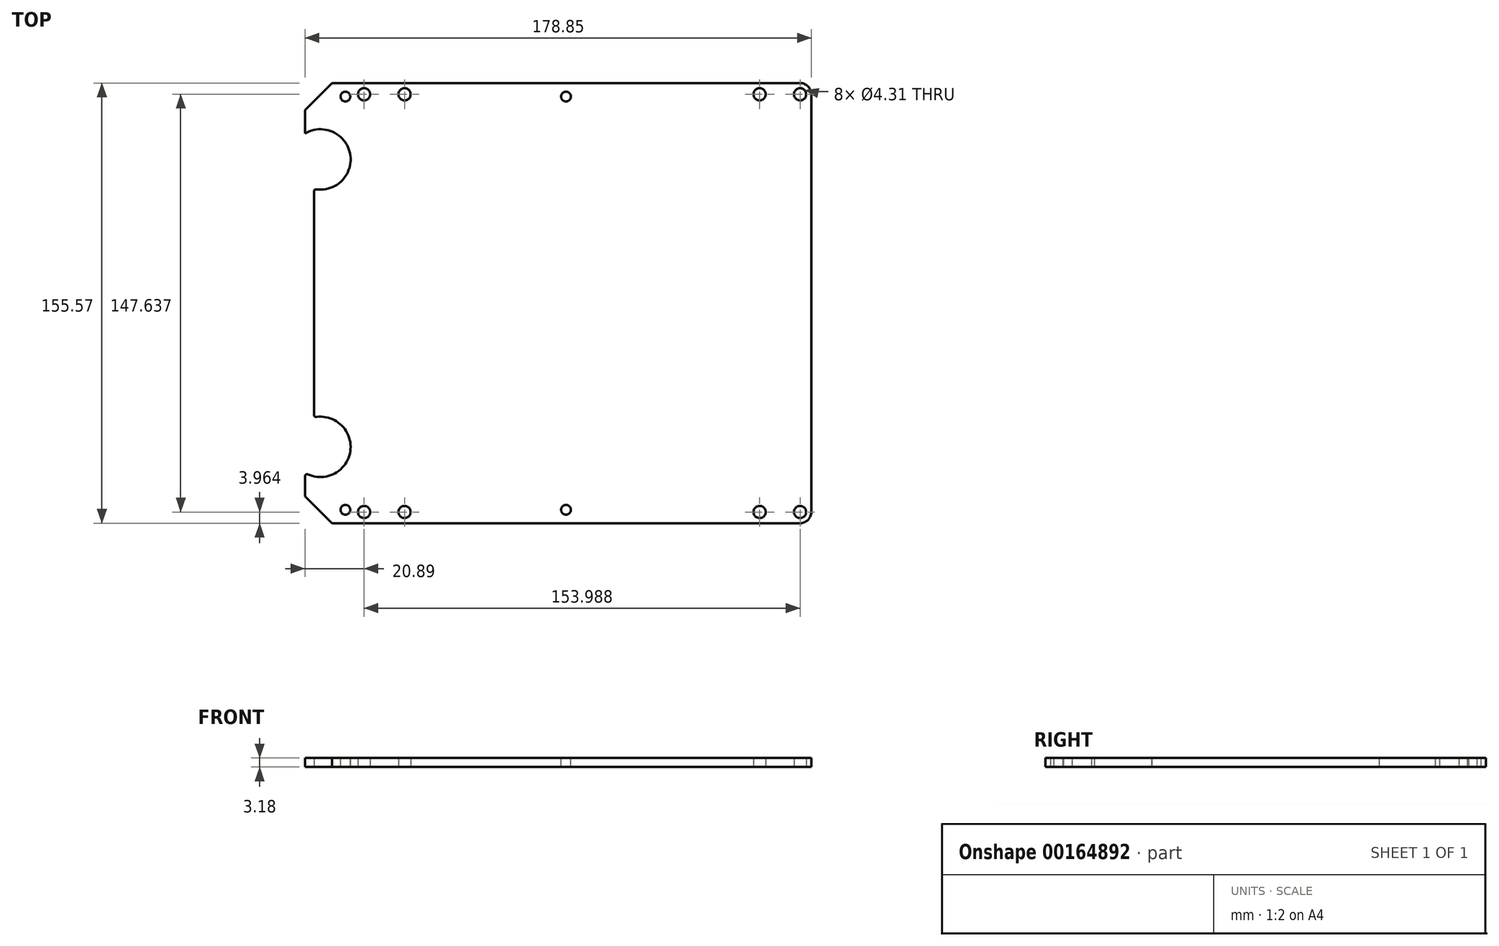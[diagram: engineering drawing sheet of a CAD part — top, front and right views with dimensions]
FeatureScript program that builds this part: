
annotation { "Feature Type Name" : "Feature", "Feature Type Description" : "" }
export const myFeature = defineFeature(function(context is Context, id is Id, definition is map)
    precondition{}
    {
        {
            var Q0;
            Q0=qCreatedBy(makeId("Top.planeOp"),FACE);
            var sketch = newSketch(context, id + "F0", { "sketchPlane" : qUnion([Q0])});
            skLineSegment(sketch, "E0.bottom", {"start": v(0, 0) * mm, "end": v(178.85, 0) * mm});
            skLineSegment(sketch, "E0.top", {"start": v(0, -155.58) * mm, "end": v(178.85, -155.58) * mm});
            skLineSegment(sketch, "E0.left", {"start": v(0, 0) * mm, "end": v(0, -155.57) * mm});
            skLineSegment(sketch, "E0.right", {"start": v(178.85, 0) * mm, "end": v(178.85, -155.58) * mm});
            skLineSegment(sketch, "E1.bottom", {"start": v(160.6, -151.6) * mm, "end": v(174.88, -151.6) * mm, "construction": true});
            skLineSegment(sketch, "E1.top", {"start": v(160.6, -3.97) * mm, "end": v(174.88, -3.97) * mm, "construction": true});
            skLineSegment(sketch, "E1.left", {"start": v(160.6, -151.6) * mm, "end": v(160.6, -3.97) * mm, "construction": true});
            skLineSegment(sketch, "E1.right", {"start": v(174.88, -151.6) * mm, "end": v(174.88, -3.97) * mm, "construction": true});
            skPoint(sketch, "E1.middle", {"position": v(167.73, -77.79) * mm});
            skLineSegment(sketch, "E2.bottom", {"start": v(20.9, -3.97) * mm, "end": v(35.18, -3.97) * mm, "construction": true});
            skLineSegment(sketch, "E2.top", {"start": v(20.9, -151.6) * mm, "end": v(35.18, -151.6) * mm, "construction": true});
            skLineSegment(sketch, "E2.left", {"start": v(20.9, -3.97) * mm, "end": v(20.9, -151.6) * mm, "construction": true});
            skLineSegment(sketch, "E2.right", {"start": v(35.18, -3.97) * mm, "end": v(35.18, -151.6) * mm, "construction": true});
            skPoint(sketch, "E2.middle", {"position": v(28.03, -77.79) * mm});
            skLineSegment(sketch, "E3", {"start": v(28.03, -77.79) * mm, "end": v(97.88, -77.79) * mm, "construction": true});
            skLineSegment(sketch, "E4", {"start": v(97.88, -77.79) * mm, "end": v(97.88, -155.58) * mm, "construction": true});
            skLineSegment(sketch, "E5", {"start": v(97.88, -77.79) * mm, "end": v(97.88, 0) * mm, "construction": true});
            skLineSegment(sketch, "E6", {"start": v(97.88, -77.79) * mm, "end": v(167.73, -77.79) * mm, "construction": true});
            skLineSegment(sketch, "E7", {"start": v(174.88, -3.97) * mm, "end": v(174.88, 0) * mm, "construction": true});
            skLineSegment(sketch, "E8", {"start": v(174.88, -3.97) * mm, "end": v(178.85, -3.97) * mm, "construction": true});
            skCircle(sketch, "E9", {"center": v(20.9, -3.97) * mm, "radius": 2.15 * mm});
            skCircle(sketch, "E10", {"center": v(35.18, -3.97) * mm, "radius": 2.15 * mm});
            skCircle(sketch, "E11", {"center": v(174.88, -3.97) * mm, "radius": 2.15 * mm});
            skCircle(sketch, "E12", {"center": v(160.6, -3.97) * mm, "radius": 2.15 * mm});
            skCircle(sketch, "E13", {"center": v(160.6, -151.6) * mm, "radius": 2.15 * mm});
            skCircle(sketch, "E14", {"center": v(174.88, -151.6) * mm, "radius": 2.15 * mm});
            skCircle(sketch, "E15", {"center": v(20.9, -151.6) * mm, "radius": 2.15 * mm});
            skCircle(sketch, "E16", {"center": v(35.18, -151.6) * mm, "radius": 2.15 * mm});
            skSolve(sketch);
        }
        {
            var Q0;
            Q0 = qSketchRegion(id + "F0", true);
            extrude(context, id + "F1", {"entities" : qUnion([Q0]), "depth" : 3.17 * mm});
        }
        {
            var Q0;
            Q0=makeQuery(id+"F1.opExtrude","SWEPT_EDGE",EDGE,{"disambiguationData":[OSD([sQuery(id+"F0.wireOp",EDGE,"E0.bottom"),sQuery(id+"F0.wireOp",EDGE,"E0.right")])]});
            var Q1;
            Q1=makeQuery(id+"F1.opExtrude","SWEPT_EDGE",EDGE,{"disambiguationData":[OSD([sQuery(id+"F0.wireOp",EDGE,"E0.top"),sQuery(id+"F0.wireOp",EDGE,"E0.right")])]});
            fillet(context, id + "F2", {"entities" : qUnion([Q0, Q1]), "radius" : 3.97 * mm, "tangentPropagation" : true, "allowEdgeOverflow" : false});
        }
        {
            var Q0;
            Q0=makeQuery(id+"F1.opExtrude","CAP_FACE",FACE,{"disambiguationData":[OSD([sQuery(id+"F0.wireOp",EDGE,"E0.bottom"),sQuery(id+"F0.wireOp",EDGE,"E0.top"),sQuery(id+"F0.wireOp",EDGE,"E0.left"),sQuery(id+"F0.wireOp",EDGE,"E0.right"),sQuery(id+"F0.wireOp",EDGE,"E9"),sQuery(id+"F0.wireOp",EDGE,"E10"),sQuery(id+"F0.wireOp",EDGE,"E11"),sQuery(id+"F0.wireOp",EDGE,"E12"),sQuery(id+"F0.wireOp",EDGE,"E13"),sQuery(id+"F0.wireOp",EDGE,"E14"),sQuery(id+"F0.wireOp",EDGE,"E15"),sQuery(id+"F0.wireOp",EDGE,"E16")])],"isStart":false});
            var sketch = newSketch(context, id + "F3", { "sketchPlane" : qUnion([Q0])});
            skLineSegment(sketch, "E17", {"start": v(5.45, -77.79) * mm, "end": v(0, -77.79) * mm, "construction": true});
            skLineSegment(sketch, "E18", {"start": v(5.45, -26.99) * mm, "end": v(5.45, -128.59) * mm, "construction": true});
            skArc(sketch, "E19", {"start": v(0, -137.76) * mm, "mid": v(16, -130.3) * mm, "end": v(3.18, -118.16) * mm});
            skLineSegment(sketch, "E20", {"start": v(0, -17.81) * mm, "end": v(0, -137.76) * mm});
            skArc(sketch, "E21", {"start": v(3.17, -37.42) * mm, "mid": v(16, -25.28) * mm, "end": v(0, -17.81) * mm});
            skLineSegment(sketch, "E22", {"start": v(5.45, -128.59) * mm, "end": v(0, -128.59) * mm, "construction": true});
            skLineSegment(sketch, "E23", {"start": v(3.17, -37.42) * mm, "end": v(3.18, -118.16) * mm});
            skSolve(sketch);
        }
        {
            var Q0;
            Q0 = qSketchRegion(id + "F3", true);
            var Q1;
            Q1=makeQuery(id+"F1.opExtrude","CAP_FACE",FACE,{"disambiguationData":[OSD([sQuery(id+"F0.wireOp",EDGE,"E0.bottom"),sQuery(id+"F0.wireOp",EDGE,"E0.top"),sQuery(id+"F0.wireOp",EDGE,"E0.left"),sQuery(id+"F0.wireOp",EDGE,"E0.right"),sQuery(id+"F0.wireOp",EDGE,"E9"),sQuery(id+"F0.wireOp",EDGE,"E10"),sQuery(id+"F0.wireOp",EDGE,"E11"),sQuery(id+"F0.wireOp",EDGE,"E12"),sQuery(id+"F0.wireOp",EDGE,"E13"),sQuery(id+"F0.wireOp",EDGE,"E14"),sQuery(id+"F0.wireOp",EDGE,"E15"),sQuery(id+"F0.wireOp",EDGE,"E16")])],"isStart":true});
            extrude(context, id + "F4", {"entities" : qUnion([Q0]), "operationType" : NewBodyOperationType.REMOVE, "endBound" : BoundingType.UP_TO_SURFACE, "oppositeDirection" : true, "endBoundEntityFace" : qUnion([Q1]), "depth" : 25.4 * mm});
        }
        {
            var Q0;
            {var subQ0=sQuery(id+"F3.wireOp",EDGE,"wcZEUR4v-bPc0-u3v2-X1AI-emrUXp2CaUBA");var subQ1=sQuery(id+"F3.wireOp",EDGE,"E21");var subQ2=sQuery(id+"F0.wireOp",EDGE,"E0.left");Q0=makeQuery(id+"F4.boolean.opBoolean","COPY",EDGE,{"derivedFrom":makeQuery(id+"F4.opExtrude","SWEPT_EDGE",EDGE,{"disambiguationData":[OSD([subQ2,subQ1,subQ0]),TDD([makeQuery(id+"F3.imprint","INTERSECT",VERTEX,{"disambiguationData":[OD(1.0)],"derivedFrom":[makeQuery(id+"F1.opExtrude","CAP_EDGE",EDGE,{"disambiguationData":[OSD([subQ2])],"isStart":false}),subQ1,subQ0]})])]})});}
            var Q1;
            {var subQ0=sQuery(id+"F3.wireOp",EDGE,"wcZEUR4v-bPc0-u3v2-X1AI-emrUXp2CaUBA");var subQ1=sQuery(id+"F3.wireOp",EDGE,"E21");var subQ2=sQuery(id+"F0.wireOp",EDGE,"E0.left");Q1=makeQuery(id+"F4.boolean.opBoolean","COPY",EDGE,{"derivedFrom":makeQuery(id+"F4.opExtrude","SWEPT_EDGE",EDGE,{"disambiguationData":[OSD([subQ2,subQ1,subQ0]),TDD([makeQuery(id+"F3.imprint","INTERSECT",VERTEX,{"disambiguationData":[OD(0.0)],"derivedFrom":[makeQuery(id+"F1.opExtrude","CAP_EDGE",EDGE,{"disambiguationData":[OSD([subQ2])],"isStart":false}),subQ1,subQ0]})])]})});}
            var Q2;
            {var subQ0=sQuery(id+"F3.wireOp",EDGE,"E20");var subQ1=sQuery(id+"F3.wireOp",EDGE,"E19");var subQ2=sQuery(id+"F0.wireOp",EDGE,"E0.left");Q2=makeQuery(id+"F4.boolean.opBoolean","COPY",EDGE,{"derivedFrom":makeQuery(id+"F4.opExtrude","SWEPT_EDGE",EDGE,{"disambiguationData":[OSD([subQ2,subQ1,subQ0]),TDD([makeQuery(id+"F3.imprint","INTERSECT",VERTEX,{"disambiguationData":[OD(1.0)],"derivedFrom":[makeQuery(id+"F1.opExtrude","CAP_EDGE",EDGE,{"disambiguationData":[OSD([subQ2])],"isStart":false}),subQ1,subQ0]})])]})});}
            var Q3;
            {var subQ0=sQuery(id+"F3.wireOp",EDGE,"E20");var subQ1=sQuery(id+"F3.wireOp",EDGE,"E19");var subQ2=sQuery(id+"F0.wireOp",EDGE,"E0.left");Q3=makeQuery(id+"F4.boolean.opBoolean","COPY",EDGE,{"derivedFrom":makeQuery(id+"F4.opExtrude","SWEPT_EDGE",EDGE,{"disambiguationData":[OSD([subQ2,subQ1,subQ0]),TDD([makeQuery(id+"F3.imprint","INTERSECT",VERTEX,{"disambiguationData":[OD(0.0)],"derivedFrom":[makeQuery(id+"F1.opExtrude","CAP_EDGE",EDGE,{"disambiguationData":[OSD([subQ2])],"isStart":false}),subQ1,subQ0]})])]})});}
            var Q4;
            Q4=makeQuery(id+"F4.boolean.opBoolean","COPY",EDGE,{"derivedFrom":makeQuery(id+"F4.opExtrude","SWEPT_EDGE",EDGE,{"disambiguationData":[OSD([sQuery(id+"F3.wireOp",EDGE,"E21"),sQuery(id+"F3.wireOp",EDGE,"E23")])]})});
            var Q5;
            Q5=makeQuery(id+"F4.boolean.opBoolean","COPY",EDGE,{"derivedFrom":makeQuery(id+"F4.opExtrude","SWEPT_EDGE",EDGE,{"disambiguationData":[OSD([sQuery(id+"F3.wireOp",EDGE,"E19"),sQuery(id+"F3.wireOp",EDGE,"E23")])]})});
            fillet(context, id + "F5", {"entities" : qUnion([Q0, Q1, Q2, Q3, Q4, Q5]), "radius" : 0.76 * mm, "tangentPropagation" : true, "allowEdgeOverflow" : false});
        }
        {
            var Q0;
            Q0=makeQuery(id+"F1.opExtrude","SWEPT_EDGE",EDGE,{"disambiguationData":[OSD([sQuery(id+"F0.wireOp",EDGE,"E0.bottom"),sQuery(id+"F0.wireOp",EDGE,"E0.left")])]});
            var Q1;
            Q1=makeQuery(id+"F1.opExtrude","SWEPT_EDGE",EDGE,{"disambiguationData":[OSD([sQuery(id+"F0.wireOp",EDGE,"E0.top"),sQuery(id+"F0.wireOp",EDGE,"E0.left")])]});
            chamfer(context, id + "F6", {"entities" : qUnion([Q0, Q1]), "width" : 9.52 * mm, "tangentPropagation" : true});
        }
        {
            var Q0;
            Q0=makeQuery(id+"F1.opExtrude","CAP_FACE",FACE,{"disambiguationData":[OSD([sQuery(id+"F0.wireOp",EDGE,"E0.bottom"),sQuery(id+"F0.wireOp",EDGE,"E0.top"),sQuery(id+"F0.wireOp",EDGE,"E0.left"),sQuery(id+"F0.wireOp",EDGE,"E0.right"),sQuery(id+"F0.wireOp",EDGE,"E9"),sQuery(id+"F0.wireOp",EDGE,"E10"),sQuery(id+"F0.wireOp",EDGE,"E11"),sQuery(id+"F0.wireOp",EDGE,"E12"),sQuery(id+"F0.wireOp",EDGE,"E13"),sQuery(id+"F0.wireOp",EDGE,"E14"),sQuery(id+"F0.wireOp",EDGE,"E15"),sQuery(id+"F0.wireOp",EDGE,"E16")])],"isStart":false});
            var sketch = newSketch(context, id + "F7", { "sketchPlane" : qUnion([Q0])});
            skLineSegment(sketch, "E24", {"start": v(9.52, 0) * mm, "end": v(9.52, -4.76) * mm, "construction": true});
            skLineSegment(sketch, "E25", {"start": v(9.52, -4.76) * mm, "end": v(14.29, -4.76) * mm, "construction": true});
            skLineSegment(sketch, "E26", {"start": v(3.17, -77.79) * mm, "end": v(53.24, -77.79) * mm, "construction": true});
            skLineSegment(sketch, "E27", {"start": v(92.2, 0) * mm, "end": v(92.2, -4.76) * mm, "construction": true});
            skLineSegment(sketch, "E28.bottom", {"start": v(14.29, -4.76) * mm, "end": v(92.2, -4.76) * mm, "construction": true});
            skLineSegment(sketch, "E28.top", {"start": v(14.29, -150.81) * mm, "end": v(92.2, -150.81) * mm, "construction": true});
            skLineSegment(sketch, "E28.left", {"start": v(14.29, -4.76) * mm, "end": v(14.29, -150.81) * mm, "construction": true});
            skLineSegment(sketch, "E28.right", {"start": v(92.2, -4.76) * mm, "end": v(92.2, -150.81) * mm, "construction": true});
            skPoint(sketch, "E28.middle", {"position": v(53.24, -77.79) * mm});
            skCircle(sketch, "E29", {"center": v(92.2, -4.76) * mm, "radius": 1.73 * mm});
            skCircle(sketch, "E30", {"center": v(14.29, -4.76) * mm, "radius": 1.73 * mm});
            skCircle(sketch, "E31", {"center": v(14.29, -150.81) * mm, "radius": 1.73 * mm});
            skCircle(sketch, "E32", {"center": v(92.2, -150.81) * mm, "radius": 1.73 * mm});
            skSolve(sketch);
        }
        {
            var Q0;
            Q0 = qSketchRegion(id + "F7", true);
            var Q1;
            Q1=makeQuery(id+"F1.opExtrude","CAP_FACE",FACE,{"disambiguationData":[OSD([sQuery(id+"F0.wireOp",EDGE,"E0.bottom"),sQuery(id+"F0.wireOp",EDGE,"E0.top"),sQuery(id+"F0.wireOp",EDGE,"E0.left"),sQuery(id+"F0.wireOp",EDGE,"E0.right"),sQuery(id+"F0.wireOp",EDGE,"E9"),sQuery(id+"F0.wireOp",EDGE,"E10"),sQuery(id+"F0.wireOp",EDGE,"E11"),sQuery(id+"F0.wireOp",EDGE,"E12"),sQuery(id+"F0.wireOp",EDGE,"E13"),sQuery(id+"F0.wireOp",EDGE,"E14"),sQuery(id+"F0.wireOp",EDGE,"E15"),sQuery(id+"F0.wireOp",EDGE,"E16")])],"isStart":true});
            extrude(context, id + "F8", {"entities" : qUnion([Q0]), "operationType" : NewBodyOperationType.REMOVE, "endBound" : BoundingType.UP_TO_SURFACE, "oppositeDirection" : true, "endBoundEntityFace" : qUnion([Q1]), "depth" : 25.4 * mm});
        }
    });
